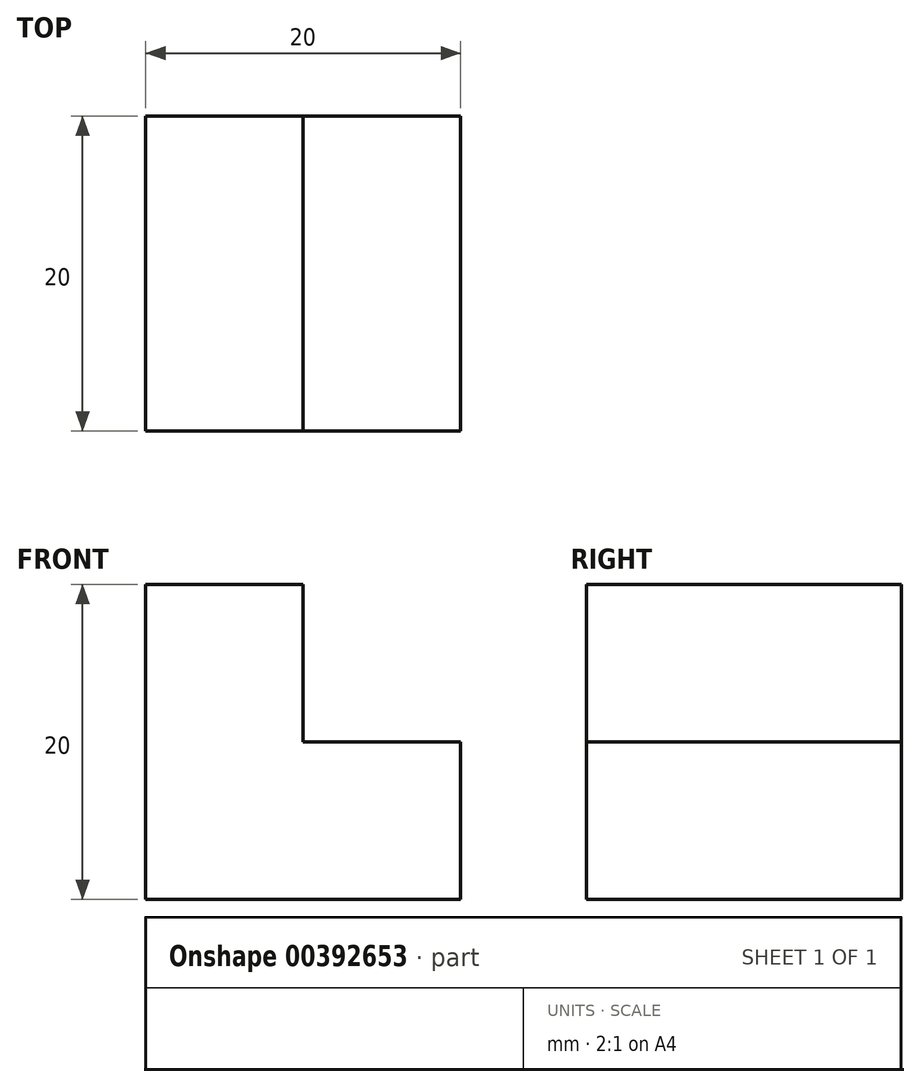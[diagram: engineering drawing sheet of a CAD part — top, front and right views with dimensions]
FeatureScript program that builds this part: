
annotation { "Feature Type Name" : "Feature", "Feature Type Description" : "" }
export const myFeature = defineFeature(function(context is Context, id is Id, definition is map)
    precondition{}
    {
        {
            var Q0;
            Q0=qCreatedBy(makeId("Top.planeOp"),FACE);
            var sketch = newSketch(context, id + "F0", { "sketchPlane" : qUnion([Q0])});
            skLineSegment(sketch, "E0.bottom", {"start": v(10, -10) * mm, "end": v(-10, -10) * mm});
            skLineSegment(sketch, "E0.top", {"start": v(10, 10) * mm, "end": v(-10, 10) * mm});
            skLineSegment(sketch, "E0.left", {"start": v(10, -10) * mm, "end": v(10, 10) * mm});
            skLineSegment(sketch, "E0.right", {"start": v(-10, -10) * mm, "end": v(-10, 10) * mm});
            skPoint(sketch, "E0.middle", {"position": v(0, 0) * mm});
            skLineSegment(sketch, "E1", {"start": v(0, 10) * mm, "end": v(0, -10) * mm});
            skSolve(sketch);
        }
        {
            var Q0;
            {var subQ0=sQuery(id+"F0.wireOp",EDGE,"E0.right");Q0=makeQuery(id+"F0.imprint","IMPRINT",FACE,{"disambiguationData":[TD([[makeQuery(id+"F0.imprint","IMPRINT",EDGE,{"derivedFrom":subQ0}),-1.0]])]});}
            extrude(context, id + "F1", {"entities" : qUnion([Q0]), "depth" : 20 * mm});
        }
        {
            var Q0;
            {var subQ0=sQuery(id+"F0.wireOp",EDGE,"E0.left");Q0=makeQuery(id+"F0.imprint","IMPRINT",FACE,{"disambiguationData":[TD([[makeQuery(id+"F0.imprint","IMPRINT",EDGE,{"derivedFrom":subQ0}),1.0]])]});}
            extrude(context, id + "F2", {"entities" : qUnion([Q0]), "operationType" : NewBodyOperationType.ADD, "depth" : 10 * mm});
        }
    });
